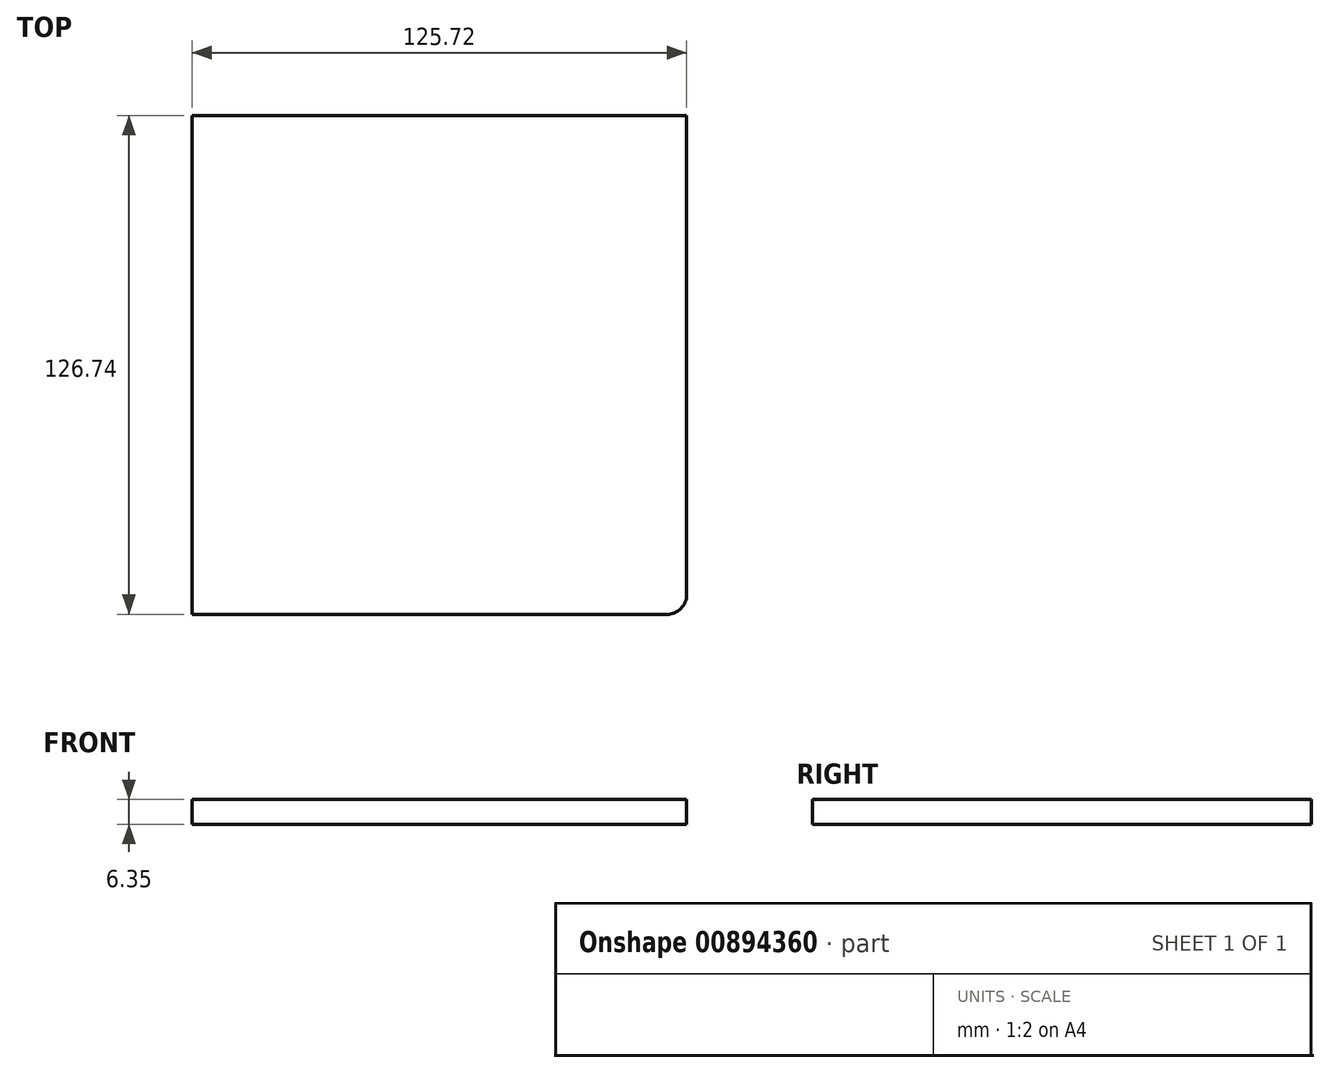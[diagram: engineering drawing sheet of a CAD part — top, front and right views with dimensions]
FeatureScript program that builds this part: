
annotation { "Feature Type Name" : "Feature", "Feature Type Description" : "" }
export const myFeature = defineFeature(function(context is Context, id is Id, definition is map)
    precondition{}
    {
        {
            var Q0;
            Q0=qCreatedBy(makeId("Top.planeOp"),FACE);
            var sketch = newSketch(context, id + "F0", { "sketchPlane" : qUnion([Q0])});
            skLineSegment(sketch, "E0.bottom", {"start": v(62.86, 63.37) * mm, "end": v(-62.86, 63.37) * mm});
            skLineSegment(sketch, "E0.top", {"start": v(62.86, -63.37) * mm, "end": v(-62.86, -63.37) * mm});
            skLineSegment(sketch, "E0.left", {"start": v(62.86, 63.37) * mm, "end": v(62.86, -63.37) * mm});
            skLineSegment(sketch, "E0.right", {"start": v(-62.86, 63.37) * mm, "end": v(-62.86, -63.37) * mm});
            skPoint(sketch, "E0.middle", {"position": v(0, 0) * mm});
            skSolve(sketch);
        }
        {
            var Q0;
            Q0=makeQuery(id+"F0.imprint","IMPRINT",FACE,{"disambiguationData":[TD([[makeQuery(id+"F0.imprint","IMPRINT",EDGE,{"derivedFrom":sQuery(id+"F0.wireOp",EDGE,"E0.bottom")}),1.0]])]});
            extrude(context, id + "F1", {"entities" : qUnion([Q0]), "depth" : 6.35 * mm, "offsetDistance" : 25.4 * mm});
        }
        {
            var Q0;
            Q0=makeQuery(id+"F1.opExtrude","SWEPT_EDGE",EDGE,{"disambiguationData":[OSD([sQuery(id+"F0.wireOp",EDGE,"E0.top"),sQuery(id+"F0.wireOp",EDGE,"E0.left")])]});
            fillet(context, id + "F2", {"entities" : qUnion([Q0]), "radius" : 5.08 * mm, "allowEdgeOverflow" : false});
        }
    });
